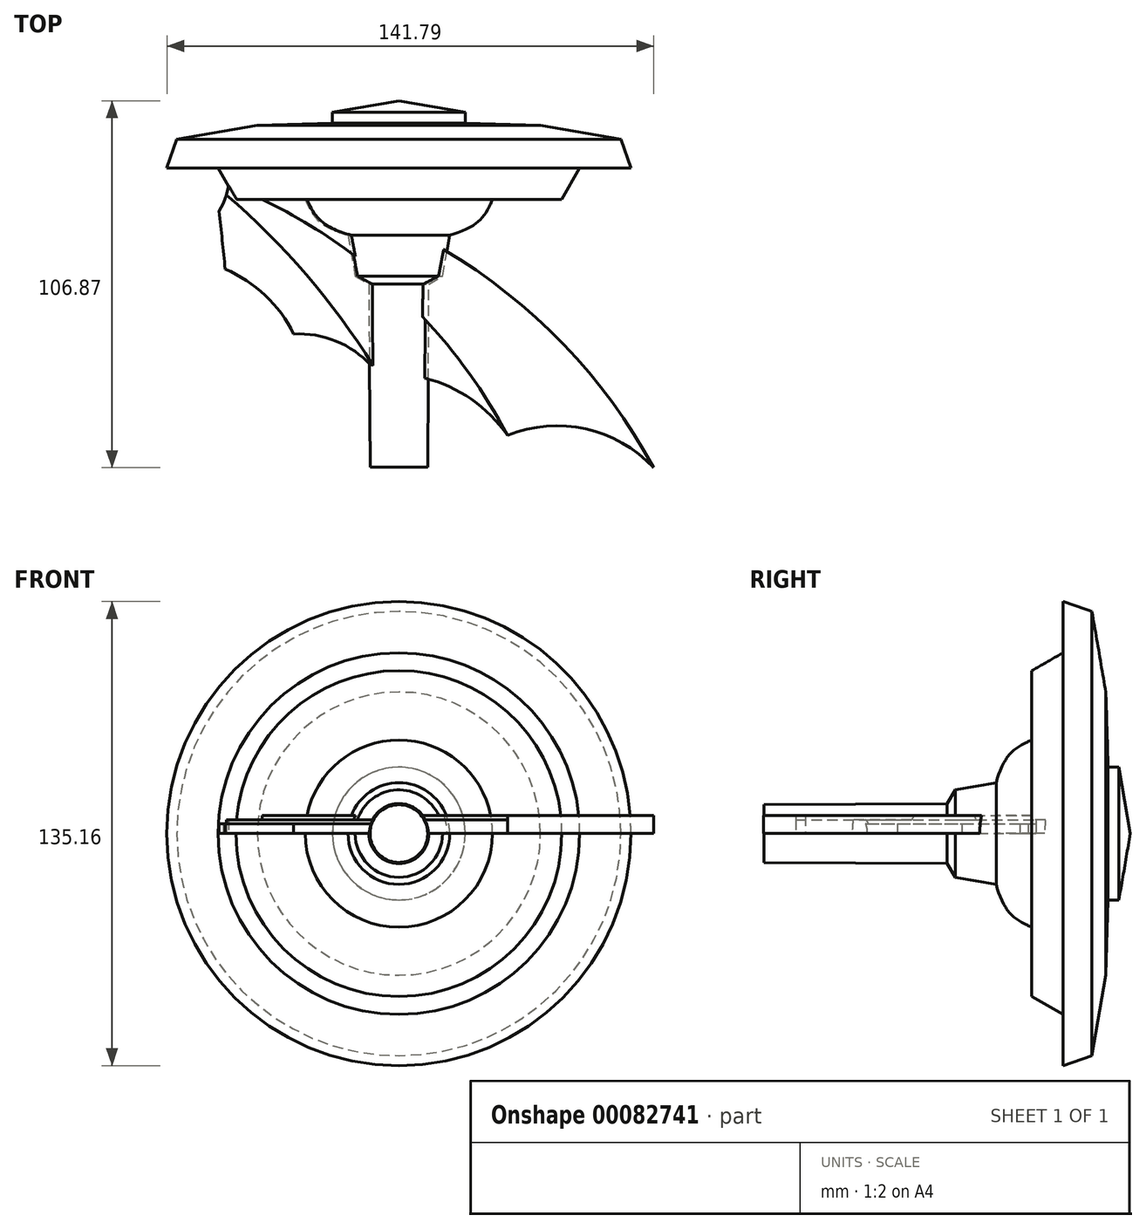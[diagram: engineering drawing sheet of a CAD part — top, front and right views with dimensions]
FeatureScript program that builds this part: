
annotation { "Feature Type Name" : "Feature", "Feature Type Description" : "" }
export const myFeature = defineFeature(function(context is Context, id is Id, definition is map)
    precondition{}
    {
        {
            var Q0;
            Q0=qCreatedBy(makeId("Top.planeOp"),FACE);
            var sketch = newSketch(context, id + "F0", { "sketchPlane" : qUnion([Q0])});
            skArc(sketch, "E0", {"start": v(31.69, -28.65) * mm, "mid": v(-2.44, 15.05) * mm, "end": v(-49.5, 44.39) * mm});
            skArc(sketch, "E1", {"start": v(74.21, -38.04) * mm, "mid": v(22.6, 19.39) * mm, "end": v(-49.5, 47.01) * mm});
            skArc(sketch, "E2", {"start": v(-6.01, -10.81) * mm, "mid": v(-25.99, 17.06) * mm, "end": v(-50.19, 41.35) * mm});
            skArc(sketch, "E3", {"start": v(-30.64, 0.9) * mm, "mid": v(-40.2, 20.33) * mm, "end": v(-51.15, 39) * mm});
            skArc(sketch, "E4", {"start": v(-50.6, 19.81) * mm, "mid": v(-51.45, 28.24) * mm, "end": v(-52.4, 36.66) * mm});
            skArc(sketch, "E5", {"start": v(-30.64, 0.9) * mm, "mid": v(-38.92, 12.15) * mm, "end": v(-50.6, 19.81) * mm});
            skArc(sketch, "E6", {"start": v(-6.01, -10.81) * mm, "mid": v(-16.83, -1.82) * mm, "end": v(-30.64, 0.9) * mm});
            skArc(sketch, "E7", {"start": v(31.69, -28.65) * mm, "mid": v(15.22, -14.7) * mm, "end": v(-6.01, -10.81) * mm});
            skArc(sketch, "E8", {"start": v(74.21, -38.04) * mm, "mid": v(54.4, -26.76) * mm, "end": v(31.69, -28.65) * mm});
            skLineSegment(sketch, "E9", {"start": v(-52.4, 36.66) * mm, "end": v(-51.15, 39) * mm});
            skLineSegment(sketch, "E10", {"start": v(-51.15, 39) * mm, "end": v(-50.19, 41.35) * mm});
            skLineSegment(sketch, "E11", {"start": v(-49.5, 44.39) * mm, "end": v(-50.19, 41.35) * mm});
            skLineSegment(sketch, "E12", {"start": v(-49.5, 44.39) * mm, "end": v(-49.5, 47.01) * mm});
            skSolve(sketch);
        }
        {
            var Q0;
            Q0=makeQuery(id+"F0.imprint","IMPRINT",FACE,{"disambiguationData":[TD([[makeQuery(id+"F0.imprint","IMPRINT",EDGE,{"derivedFrom":sQuery(id+"F0.wireOp",EDGE,"E0")}),-1.0]])]});
            var Q1;
            Q1=makeQuery(id+"F0.imprint","IMPRINT",FACE,{"disambiguationData":[TD([[makeQuery(id+"F0.imprint","IMPRINT",EDGE,{"derivedFrom":sQuery(id+"F0.wireOp",EDGE,"E2")}),1.0]])]});
            var Q2;
            Q2=makeQuery(id+"F0.imprint","IMPRINT",FACE,{"disambiguationData":[TD([[makeQuery(id+"F0.imprint","IMPRINT",EDGE,{"derivedFrom":sQuery(id+"F0.wireOp",EDGE,"E3")}),1.0]])]});
            extrude(context, id + "F1", {"entities" : qUnion([Q0, Q1, Q2]), "depth" : 2.92 * mm});
        }
        {
            var Q0;
            Q0=makeQuery(id+"F0.imprint","IMPRINT",FACE,{"disambiguationData":[TD([[makeQuery(id+"F0.imprint","IMPRINT",EDGE,{"derivedFrom":sQuery(id+"F0.wireOp",EDGE,"E0")}),1.0]])]});
            extrude(context, id + "F2", {"entities" : qUnion([Q0]), "depth" : 4.04 * mm});
        }
        {
            var Q0;
            Q0=makeQuery(id+"F1.opExtrude","CAP_FACE",FACE,{"disambiguationData":[OSD([sQuery(id+"F0.wireOp",EDGE,"E0"),sQuery(id+"F0.wireOp",EDGE,"E1"),sQuery(id+"F0.wireOp",EDGE,"E8"),sQuery(id+"F0.wireOp",EDGE,"E12")])],"isStart":false});
            extrude(context, id + "F3", {"entities" : qUnion([Q0]), "operationType" : NewBodyOperationType.ADD, "depth" : 2.31 * mm});
        }
        {
            var Q0;
            Q0=qCreatedBy(makeId("Top.planeOp"),FACE);
            var sketch = newSketch(context, id + "F4", { "sketchPlane" : qUnion([Q0])});
            skLineSegment(sketch, "E13", {"start": v(0, 68.83) * mm, "end": v(19.35, 65.48) * mm});
            skLineSegment(sketch, "E14", {"start": v(64.68, 57.64) * mm, "end": v(67.58, 49.22) * mm});
            skLineSegment(sketch, "E15", {"start": v(67.58, 49.22) * mm, "end": v(52.67, 49.22) * mm});
            skLineSegment(sketch, "E16", {"start": v(52.67, 49.22) * mm, "end": v(47.46, 40.13) * mm});
            skLineSegment(sketch, "E17", {"start": v(47.46, 40.13) * mm, "end": v(27.27, 40.13) * mm});
            skFitSpline(sketch, "E18", {"points": [v(27.27, 40.13) * mm, v(23.4, 33.92) * mm, v(13.05, 29.36) * mm, v(0, 29.09) * mm], "startDerivative": vector(-10.32, -23.7) * mm, "endDerivative": vector(-35.17, 2) * mm});
            skLineSegment(sketch, "E19", {"start": v(0, 68.83) * mm, "end": v(0, 29.09) * mm});
            skLineSegment(sketch, "E20", {"start": v(41.24, 61.7) * mm, "end": v(64.68, 57.64) * mm});
            skLineSegment(sketch, "E21", {"start": v(19.35, 65.48) * mm, "end": v(19.35, 62.34) * mm});
            skLineSegment(sketch, "E22", {"start": v(19.35, 62.34) * mm, "end": v(41.24, 61.7) * mm});
            skLineSegment(sketch, "E23", {"start": v(8.4, -37.93) * mm, "end": v(0, -37.93) * mm});
            skLineSegment(sketch, "E24", {"start": v(0, -37.93) * mm, "end": v(0, 29.09) * mm});
            skLineSegment(sketch, "E25", {"start": v(14.8, 29.74) * mm, "end": v(12.72, 17.81) * mm});
            skLineSegment(sketch, "E26", {"start": v(12.72, 17.81) * mm, "end": v(8.74, 15.42) * mm});
            skLineSegment(sketch, "E27", {"start": v(8.75, 15.43) * mm, "end": v(8.4, -37.93) * mm});
            skSolve(sketch);
        }
        {
            var Q0;
            Q0=makeQuery(id+"F4.imprint","IMPRINT",FACE,{"disambiguationData":[TD([[makeQuery(id+"F4.imprint","IMPRINT",EDGE,{"derivedFrom":sQuery(id+"F4.wireOp",EDGE,"E13")}),-1.0]])]});
            var Q1;
            Q1=sQuery(id+"F4.wireOp",EDGE,"E19");
            revolve(context, id + "F5", {"entities" : qUnion([Q0]), "axis" : qUnion([Q1]), "revolveType" : RevolveType.FULL});
        }
        {
            var Q0;
            Q0=makeQuery(id+"F4.imprint","IMPRINT",FACE,{"disambiguationData":[TD([[makeQuery(id+"F4.imprint","IMPRINT",EDGE,{"derivedFrom":sQuery(id+"F4.wireOp",EDGE,"E18")}),1.0]])]});
            var Q1;
            Q1=sQuery(id+"F4.wireOp",EDGE,"E24");
            revolve(context, id + "F6", {"operationType" : NewBodyOperationType.ADD, "entities" : qUnion([Q0]), "axis" : qUnion([Q1]), "revolveType" : RevolveType.FULL});
        }
    });
